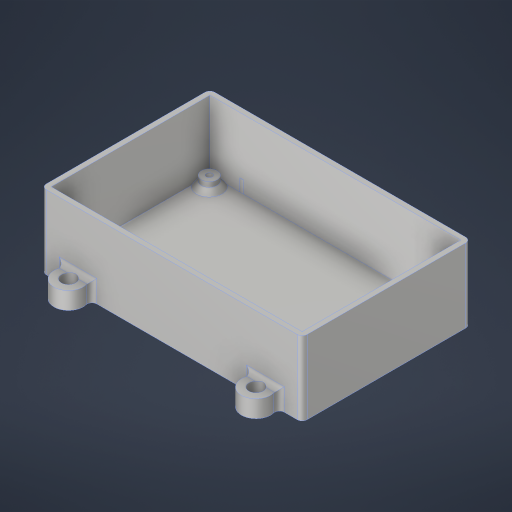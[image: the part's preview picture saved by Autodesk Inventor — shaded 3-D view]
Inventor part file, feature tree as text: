
AUTODESK INVENTOR PART (.ipt)
format: ipt  version: 2023 (Build 270158000, 158)  size: 320,000 bytes
history: native  units: in
note: dims shown in document units (in); Inventor stores cm internally (conversion verified against a paired STEP export)
features: sketch x3, extrude x3, fillet x2, shell x1, hole x1, chamfer x1, projected_geometry x1
ambient origin geometry x8: Origin, YZ Plane, XZ Plane, XY Plane, X Axis, Y Axis, Z Axis, Center Point
bodies: Solid1 (feature_tree)
feature tree (12):
  sketch  "Sketch1"  dims[d0=2.2004in d1=3.6951in d2=4.0157in d3=2.5394in]
  extrude  "Extrusion1"  Depth=3.6951in
  fillet  "Fillet1"  Radius=4.0157in
  shell  "Shell1"  Thickness=2.5394in
  hole  "Hole1"  [1 undecoded]
  extrude  "Extrusion2"  Depth=0.0787in
  chamfer  "Chamfer1"  Distance=0.0787in
  extrude  "Extrusion3"  Depth=0.0787in
  fillet  "Fillet2"  Radius=0.1575in
  sketch  "Sketch2"  dims[d4=0.0787in d5=0.0787in]
  projected_geometry  "Projected Loop1"
  sketch  "Sketch3"  dims[d6=1.1811in d7=0.0in d8=0.0787in d9=0.0787in d10=0.0968in d11=0.2362in d12=1.125in d13=0.0787in d14=0.5635in d15=0.315in d16=0.8108in d17=0.0787in d18=0.1575in d19=0.0in d20=0.0787in d21=0.0787in d22=45.0deg d23=3.0in d24=3.0in d25=0.2283in d26=0.1181in d27=0.2756in d28=0.0in d29=0.0787in]
note: 1 required parameter value undecoded (feature->parameter linkage not recoverable at this tier; creation-order binding heuristic only, values carry confidence <= 0.55)
